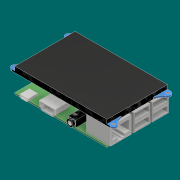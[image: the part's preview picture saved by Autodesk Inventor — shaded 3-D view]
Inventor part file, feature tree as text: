
AUTODESK INVENTOR PART (.ipt)
format: ipt  version: 2018 (Build 220112000, 112)  size: 571,392 bytes
history: native  units: mm
features: extrude x21, sketch x21, projected_geometry x12, plane x1
ambient origin geometry x8: Origin, YZ Plane, XZ Plane, XY Plane, X Axis, Y Axis, Z Axis, Center Point
bodies: Solid1 (feature_tree)
feature tree (55):
  extrude  "Extrusion1"  Depth=56.0mm
  extrude  "Extrusion2"  Depth=3.7mm TaperAngle=0.0deg
  plane  "Work Plane1"
  extrude  "Extrusion3"  Depth=2.5mm
  extrude  "Extrusion4"  Depth=16.0mm
  extrude  "Extrusion5"  Depth=6.8mm
  extrude  "Extrusion6"  Depth=52.0mm
  extrude  "Extrusion7"  Depth=52.0mm
  extrude  "Extrusion8"  Depth=1.0mm
  extrude  "Extrusion9"  Depth=15.9mm
  extrude  "Extrusion10"  Depth=1.0mm
  extrude  "Extrusion11"  Depth=2.0mm TaperAngle=0.0deg
  extrude  "Extrusion12"  Depth=3.0mm
  extrude  "Extrusion13"  Depth=16.0mm
  extrude  "Extrusion14"  Depth=3.8mm
  extrude  "Extrusion15"  Depth=2.5mm
  extrude  "Extrusion16"  Depth=1.5mm
  extrude  "Extrusion17"  Depth=21.5mm TaperAngle=0.0deg
  extrude  "Extrusion18"  Depth=1.0mm TaperAngle=0.0deg
  extrude  "Extrusion19"  Depth=6.0mm
  extrude  "Extrusion20"  Depth=18.0mm TaperAngle=0.0deg
  extrude  "Extrusion21"  Depth=6.0mm
  sketch  "Sketch1"  dims[d0=85.5mm d1=56.0mm]
  sketch  "Sketch2"  dims[d2=85.5mm d3=3.7mm d4=0.0mm]
  sketch  "Sketch3"  dims[d5=45.6mm d7=2.5mm]
  sketch  "Sketch4"  dims[d8=1.5mm d9=0.0mm d10=16.0mm]
  sketch  "Sketch5"  dims[d11=1.3mm d12=0.0mm d13=6.8mm]
  sketch  "Sketch6"  dims[d14=0.5mm d15=52.0mm]
  projected_geometry  "Projected Loop1"
  projected_geometry  "Projected Loop2"
  sketch  "Sketch7"  dims[d16=5.0mm d17=52.0mm]
  projected_geometry  "Projected Loop3"
  sketch  "Sketch8"  dims[d18=16.0mm d19=0.0mm d20=1.0mm]
  projected_geometry  "Projected Loop4"
  sketch  "Sketch9"  dims[d21=15.0mm d22=15.9mm]
  projected_geometry  "Projected Loop5"
  projected_geometry  "Projected Loop6"
  sketch  "Sketch10"  dims[d23=15.0mm d24=1.0mm]
  sketch  "Sketch11"  dims[d27=3.1mm]
  sketch  "Sketch12"  dims[d28=1.0mm d29=15.0mm d30=15.9mm d31=15.0mm d32=3.1mm d33=2.0mm d34=0.0mm]
  sketch  "Sketch13"  dims[d35=19.1mm d36=0.0mm d37=3.0mm]
  sketch  "Sketch14"  dims[d38=15.9mm d39=16.0mm]
  projected_geometry  "Projected Loop7"
  sketch  "Sketch15"  dims[d40=15.9mm d42=3.8mm]
  sketch  "Sketch16"  dims[d43=4.7mm d44=2.5mm]
  sketch  "Sketch17"  dims[d45=2.0mm d46=1.5mm]
  sketch  "Sketch18"  dims[d47=1.5mm d48=21.5mm d49=0.0mm]
  projected_geometry  "Projected Loop8"
  sketch  "Sketch19"  dims[d50=1.0mm d51=0.0mm d52=1.0mm d53=0.0mm]
  sketch  "Sketch20"  dims[d54=8.5mm d55=6.0mm]
  sketch  "Sketch21"  dims[d56=7.0mm d57=18.0mm d58=0.0mm d59=6.0mm d60=2.0mm d61=0.0mm d62=1.0mm d63=10.0mm d64=4.0mm d65=15.0mm d66=1.0mm d67=10.0mm d68=0.0mm d69=2.0mm d70=0.0mm d71=1.0mm d72=0.0mm d73=1.0mm d74=10.0mm d75=0.0mm d76=10.0mm d77=0.0mm d78=10.2mm d79=7.8mm d80=1.5mm d81=0.6mm d82=8.0mm d83=0.0mm d84=1.0mm d85=0.0mm d86=2.0mm d87=10.0mm d88=3.0mm d89=20.0mm d90=5.0mm d91=0.0mm d92=1.0mm d93=0.0mm d94=1.2mm d95=1.2mm d96=1.2mm d97=1.2mm d98=15.0mm d99=0.0mm]
  projected_geometry  "Projected Loop9"
  projected_geometry  "Projected Loop10"
  projected_geometry  "Projected Loop11"
  projected_geometry  "Projected Loop12"
